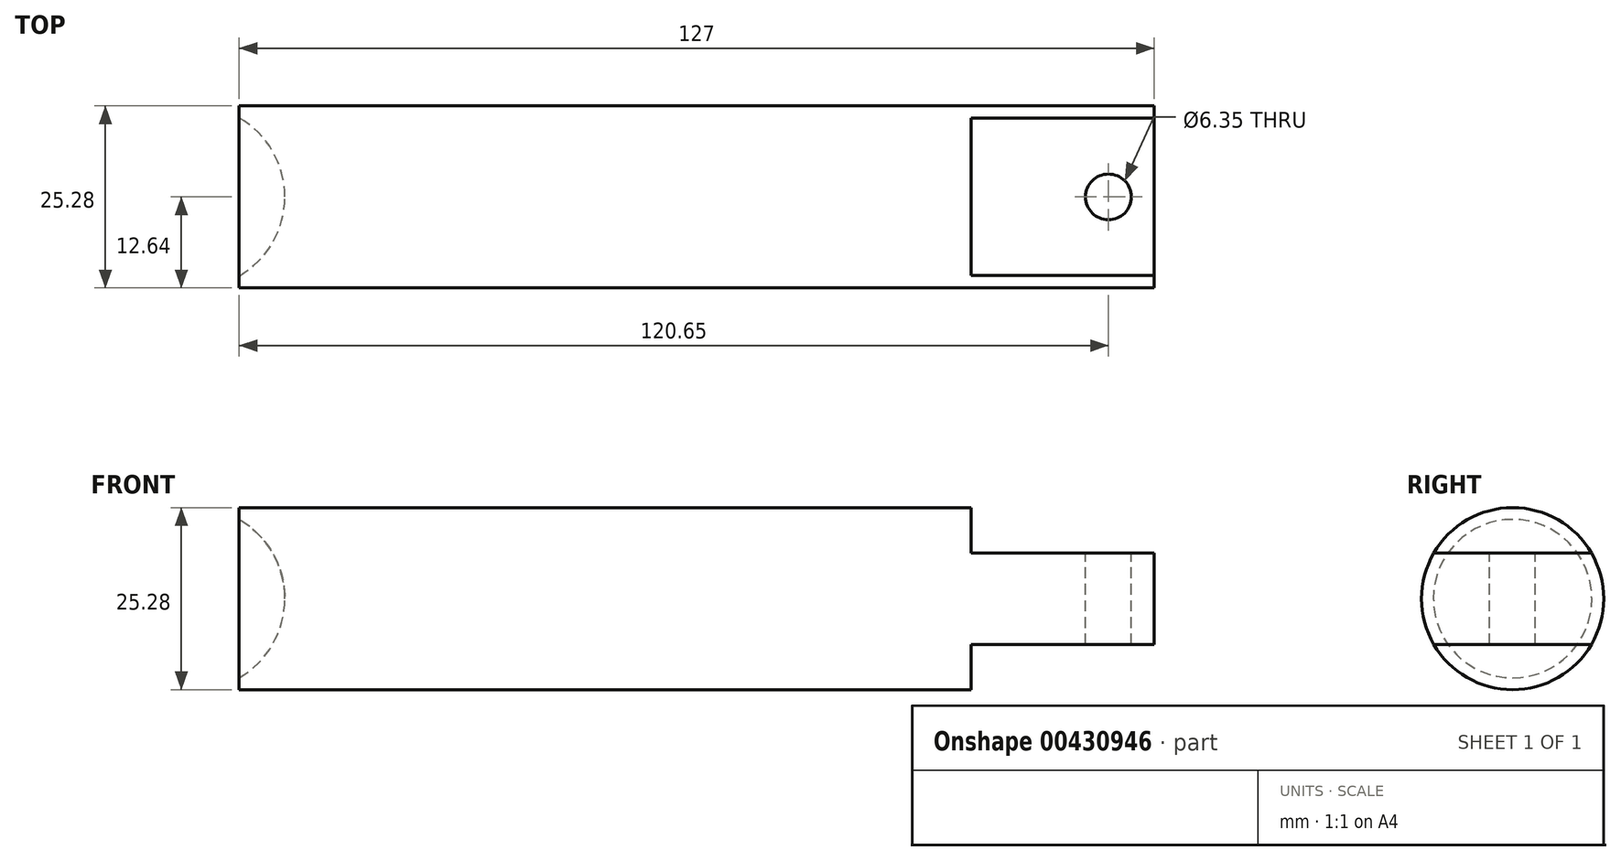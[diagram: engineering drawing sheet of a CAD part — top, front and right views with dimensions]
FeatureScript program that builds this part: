
annotation { "Feature Type Name" : "Feature", "Feature Type Description" : "" }
export const myFeature = defineFeature(function(context is Context, id is Id, definition is map)
    precondition{}
    {
        {
            var Q0;
            Q0=qCreatedBy(makeId("Top.planeOp"),FACE);
            var sketch = newSketch(context, id + "F0", { "sketchPlane" : qUnion([Q0])});
            skLineSegment(sketch, "E0.bottom", {"start": v(-63.5, 12.64) * mm, "end": v(63.5, 12.64) * mm});
            skLineSegment(sketch, "E0.top", {"start": v(-63.5, 0) * mm, "end": v(63.5, 0) * mm});
            skLineSegment(sketch, "E0.left", {"start": v(-63.5, 12.64) * mm, "end": v(-63.5, 0) * mm});
            skLineSegment(sketch, "E0.right", {"start": v(63.5, 12.64) * mm, "end": v(63.5, 0) * mm});
            skPoint(sketch, "E1", {"position": v(-63.5, 6.32) * mm});
            skPoint(sketch, "E2", {"position": v(0, 0) * mm});
            skLineSegment(sketch, "E3", {"start": v(63.5, 0) * mm, "end": v(90.06, 0) * mm});
            skSolve(sketch);
        }
        {
            var Q0;
            Q0=makeQuery(id+"F0.imprint","IMPRINT",FACE,{"disambiguationData":[TD([[makeQuery(id+"F0.imprint","IMPRINT",EDGE,{"derivedFrom":sQuery(id+"F0.wireOp",EDGE,"E0.bottom")}),-1.0]])]});
            var Q1;
            Q1=sQuery(id+"F0.wireOp",EDGE,"E3");
            revolve(context, id + "F1", {"entities" : qUnion([Q0]), "axis" : qUnion([Q1]), "revolveType" : RevolveType.FULL});
        }
        {
            var Q0;
            Q0=qCreatedBy(makeId("Front.planeOp"),FACE);
            var sketch = newSketch(context, id + "F2", { "sketchPlane" : qUnion([Q0])});
            skLineSegment(sketch, "E4.bottom", {"start": v(78.03, 30.26) * mm, "end": v(38.1, 30.26) * mm});
            skLineSegment(sketch, "E4.top", {"start": v(78.03, 6.35) * mm, "end": v(38.1, 6.35) * mm});
            skLineSegment(sketch, "E4.left", {"start": v(78.03, 30.26) * mm, "end": v(78.03, 6.35) * mm});
            skLineSegment(sketch, "E4.right", {"start": v(38.1, 30.26) * mm, "end": v(38.1, 6.35) * mm});
            skLineSegment(sketch, "E5.bottom", {"start": v(38.1, -6.35) * mm, "end": v(98.9, -6.35) * mm});
            skLineSegment(sketch, "E5.top", {"start": v(38.1, -34.84) * mm, "end": v(98.9, -34.84) * mm});
            skLineSegment(sketch, "E5.left", {"start": v(38.1, -6.35) * mm, "end": v(38.1, -34.84) * mm});
            skLineSegment(sketch, "E5.right", {"start": v(98.9, -6.35) * mm, "end": v(98.9, -34.84) * mm});
            skLineSegment(sketch, "E6", {"start": v(63.5, -12.64) * mm, "end": v(-63.5, -12.64) * mm});
            skLineSegment(sketch, "E7", {"start": v(-63.5, 12.64) * mm, "end": v(63.5, 12.64) * mm});
            skSolve(sketch);
        }
        {
            var Q0;
            {var subQ1=sQuery(id+"F2.wireOp",EDGE,"E4.bottom");Q0=makeQuery(id+"F2.imprint","IMPRINT",FACE,{"disambiguationData":[TD([[makeQuery(id+"F2.imprint","IMPRINT",EDGE,{"derivedFrom":subQ1}),1.0]])]});}
            var Q1;
            {var subQ3=sQuery(id+"F2.wireOp",EDGE,"E5.bottom");Q1=makeQuery(id+"F2.imprint","IMPRINT",FACE,{"disambiguationData":[TD([[makeQuery(id+"F2.imprint","IMPRINT",EDGE,{"derivedFrom":subQ3}),-1.0]])]});}
            extrude(context, id + "F3", {"entities" : qUnion([Q0, Q1]), "operationType" : NewBodyOperationType.REMOVE, "endBound" : BoundingType.SYMMETRIC, "depth" : 508 * mm});
        }
        {
            var Q0;
            Q0=qCreatedBy(makeId("Front.planeOp"),FACE);
            var sketch = newSketch(context, id + "F4", { "sketchPlane" : qUnion([Q0])});
            skLineSegment(sketch, "E8", {"start": v(-69.85, 12.7) * mm, "end": v(-69.85, 0) * mm});
            skArc(sketch, "E9", {"start": v(-57.15, 0) * mm, "mid": v(-60.87, 8.98) * mm, "end": v(-69.85, 12.7) * mm});
            skLineSegment(sketch, "E10", {"start": v(-69.85, 0) * mm, "end": v(-57.15, 0) * mm});
            skSolve(sketch);
        }
        {
            var Q0;
            Q0=makeQuery(id+"F4.imprint","IMPRINT",FACE,{"disambiguationData":[TD([[makeQuery(id+"F4.imprint","IMPRINT",EDGE,{"derivedFrom":sQuery(id+"F4.wireOp",EDGE,"E8")}),1.0]])]});
            var Q1;
            Q1=sQuery(id+"F4.wireOp",EDGE,"E10");
            revolve(context, id + "F5", {"operationType" : NewBodyOperationType.REMOVE, "entities" : qUnion([Q0]), "axis" : qUnion([Q1]), "revolveType" : RevolveType.FULL, "oppositeDirection" : true});
        }
        {
            var Q0;
            Q0=makeQuery(id+"F3.boolean.opBoolean","COPY",FACE,{"derivedFrom":makeQuery(id+"F3.opExtrude","SWEPT_FACE",FACE,{"disambiguationData":[OSD([sQuery(id+"F2.wireOp",EDGE,"E4.top")])]})});
            var sketch = newSketch(context, id + "F6", { "sketchPlane" : qUnion([Q0])});
            skCircle(sketch, "E11", {"center": v(57.15, 0) * mm, "radius": 3.18 * mm});
            skSolve(sketch);
        }
        {
            var Q0;
            Q0 = qSketchRegion(id + "F6", true);
            extrude(context, id + "F7", {"entities" : qUnion([Q0]), "operationType" : NewBodyOperationType.REMOVE, "endBound" : BoundingType.THROUGH_ALL, "oppositeDirection" : true, "depth" : 25.4 * mm});
        }
    });
